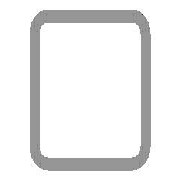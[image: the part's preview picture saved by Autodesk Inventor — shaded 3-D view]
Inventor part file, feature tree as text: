
AUTODESK INVENTOR PART (.ipt)
format: ipt  version: 2025.1 (Build 291241020, 241B)  size: 161,280 bytes
history: native  units: mm (DEFAULTED — no unit token found)
features: other x3, sketch x3, projected_geometry x2, extrude x1, plane x1
ambient origin geometry x8: Origin, YZ Plane, XZ Plane, XY Plane, X Axis, Y Axis, Z Axis, Center Point
bodies: Solid1 (feature_tree), Body (feature_tree)
feature tree (10):
  other  "Driven Length"
  other  "Start plane"
  other  "End plane"
  sketch  "Sketch5"  dims[d7=6.0mm]
  extrude  "Extrusion2"  TaperAngle=0.0deg  [1 undecoded]
  sketch  "Sketch3"  dims[d3=1000.0mm d4=0.0mm]
  plane  "Work Plane3"
  sketch  "Sketch6"  dims[d9=80.0mm d11=80.0mm d12=3.0mm d13=-0.0mm d14=1000.0mm d15=40.0mm d16=40.0mm d17=90.0deg d18=1000.0mm d22=450.0mm d24=1200.0mm d25=114.0mm d26=40.0mm d27=1200.0mm d28=310.0mm d30=397.570227mm d31=0.0mm d32=0.0mm d33=10.0mm]
  projected_geometry  "Projected Loop1"
  projected_geometry  "Projected Loop2"
note: 1 required parameter value undecoded (feature->parameter linkage not recoverable at this tier; creation-order binding heuristic only, values carry confidence <= 0.55)
